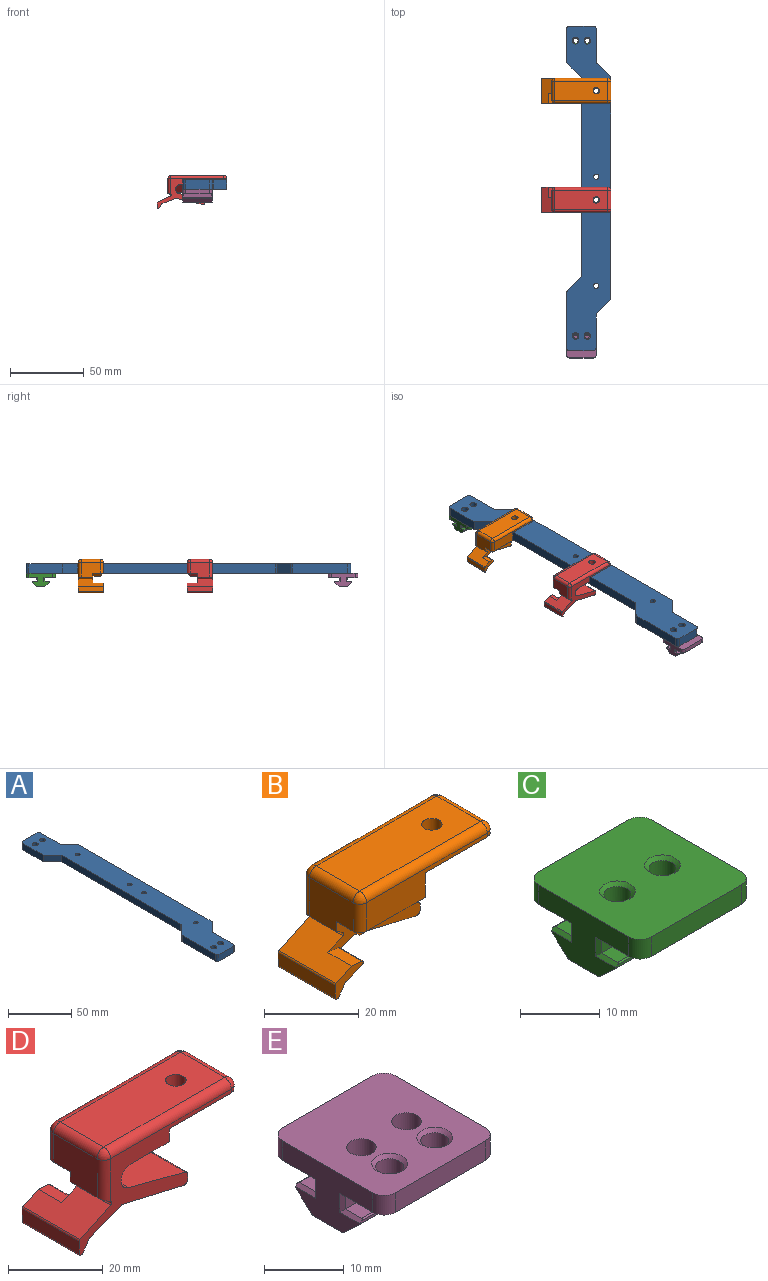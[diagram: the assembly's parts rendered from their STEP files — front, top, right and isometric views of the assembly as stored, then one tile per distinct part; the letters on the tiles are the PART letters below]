
ASSEMBLY  parts=5 mates=4
PART A: 32 faces, bbox 30x220x6.4 mm
  f0: plane 22.9x6.35mm, normal (-1,0,0), area 145.4mm2, adj f8,f9,f20,f31
  f1: plane 16x6.35mm, normal (0,-1,0), area 101.6mm2, adj f8,f9,f16,f17
  f2: plane 22.17x6.35mm, normal (1,0,0), area 140.8mm2, adj f8,f9,f16,f21
  f3: plane 148.34x6.35mm, normal (1,0,0), area 942mm2, adj f8,f9,f13,f14
  f4: plane 22.17x6.35mm, normal (1,0,0), area 140.8mm2, adj f8,f9,f18,f19
  f5: plane 16x6.35mm, normal (0,1,0), area 101.6mm2, adj f8,f9,f19,f20
  f6: plane 134.27x6.35mm, normal (-1,0,0), area 852.6mm2, adj f8,f9,f15,f31
  f7: plane 37.17x6.35mm, normal (-1,0,0), area 236mm2, adj f8,f9,f17,f22
  f8: plane 220x30mm, normal (0,0,1), area 4443.5mm2, adj f0,f1,f2,f3,f4,f5,f6,f7
  f9: plane 220x30mm, normal (0,0,-1), area 4443.5mm2, adj f0,f1,f2,f3,f4,f5,f6,f7
  f10: plane 8.83x8.83mm, normal (-0.71,0.71,0), area 79.3mm2, adj f8,f9,f15,f22
  f11: plane 8.83x8.83mm, normal (0.71,-0.71,0), area 79.3mm2, adj f8,f9,f13,f21
  f12: plane 8.83x8.83mm, normal (0.71,0.71,0), area 79.3mm2, adj f8,f9,f14,f18
  f13: cylinder r=2mm len=6.35mm, axis (0,0,1), area 10mm2, adj f3,f8,f9,f11
  f14: cylinder r=2mm len=6.35mm, axis (0,0,1), area 10mm2, adj f3,f8,f9,f12
  f15: cylinder r=2mm len=6.35mm, axis (0,0,1), area 10mm2, adj f6,f8,f9,f10
  f16: cylinder r=2mm len=6.35mm, axis (0,0,1), area 19.9mm2, adj f1,f2,f8,f9
  f17: cylinder r=2mm len=6.35mm, axis (0,0,-1), area 19.9mm2, adj f1,f7,f8,f9
  f18: cylinder r=2mm len=6.35mm, axis (0,0,1), area 10mm2, adj f4,f8,f9,f12
  f19: cylinder r=2mm len=6.35mm, axis (0,0,-1), area 19.9mm2, adj f4,f5,f8,f9
  f20: cylinder r=2mm len=6.35mm, axis (0,0,1), area 19.9mm2, adj f0,f5,f8,f9
  f21: cylinder r=2mm len=6.35mm, axis (0,0,-1), area 10mm2, adj f2,f8,f9,f11
  f22: cylinder r=2mm len=6.35mm, axis (0,0,1), area 10mm2, adj f7,f8,f9,f10
  f23: cylinder r=2.25mm len=6.35mm, axis (0,0,1), area 89.8mm2, adj f8,f9
  f24: cylinder r=2.25mm len=6.35mm, axis (0,0,1), area 89.8mm2, adj f8,f9
  f25: cylinder r=2.25mm len=6.35mm, axis (0,0,1), area 89.8mm2, adj f8,f9
  f26: cylinder r=2.25mm len=6.35mm, axis (0,0,1), area 89.8mm2, adj f8,f9
  f27: cylinder r=1.75mm len=6.35mm, axis (0,0,1), area 69.8mm2, adj f8,f9
  f28: cylinder r=1.75mm len=6.35mm, axis (0,0,1), area 69.8mm2, adj f8,f9
  f29: cylinder r=1.75mm len=6.35mm, axis (0,0,1), area 69.8mm2, adj f8,f9
  f30: cylinder r=1.75mm len=6.35mm, axis (0,0,1), area 69.8mm2, adj f8,f9
  f31: plane 10x10mm, normal (-0.71,-0.71,0), area 89.8mm2, adj f0,f6,f8,f9
PART B: 50 faces, bbox 47.4x17x22.5 mm
  f0: cylinder r=3mm len=10mm, axis (0,-1,0), area 37mm2, adj f1,f2,f8,f14,f49
  f1: cylinder r=3mm len=7.97mm, axis (0,1,0), area 28.5mm2, adj f0,f9,f14,f49
  f2: plane 27.5x10.44mm, normal (0,-1,0), area 96.4mm2, adj f0,f3,f4,f5,f6,f7,f8,f30
  f3: plane 15.5x5mm, normal (0,0,-1), area 77.5mm2, adj f2,f45,f46,f48,f49
  f4: plane 13x10mm, normal (-1,0,0), area 116.8mm2, adj f2,f5,f16,f20,f43,f45
  f5: plane 10x2.02mm, normal (-0.47,0,-0.88), area 21.9mm2, adj f2,f4,f14,f16,f37
  f6: plane 18.32x10mm, normal (-0.23,0,-0.97), area 188mm2, adj f2,f14,f36,f41
  f7: plane 10x1.26mm, normal (1,0,0), area 12.6mm2, adj f2,f14,f41,f42
  f8: plane 16.82x10mm, normal (0.25,0,0.97), area 173.8mm2, adj f0,f2,f14,f42
  f9: plane 11.31x5mm, normal (0,0,-1), area 56.6mm2, adj f1,f10,f14,f49
  f10: plane 17x6.35mm, normal (1,0,0), area 88.5mm2, adj f9,f11,f14,f15,f46,f49
  f11: plane 20.5x17mm, normal (0,0,-1), area 332.3mm2, adj f10,f12,f14,f15,f18,f25,f26
  f12: plane 13x1mm, normal (1,0,0), area 13mm2, adj f11,f18,f22,f25
  f13: plane 36x13mm, normal (0,0,1), area 453.5mm2, adj f19,f20,f22,f23,f26
  f14: plane 45.37x20.48mm, normal (0,1,0), area 226.8mm2, adj f0,f1,f5,f6,f7,f8,f9,f10
  f15: plane 36x7.35mm, normal (0,-1,0), area 147.1mm2, adj f10,f11,f23,f25,f43,f48
  f16: cylinder r=2mm len=11.07mm, axis (0,0,-1), area 32.6mm2, adj f4,f5,f14,f17
  f17: sphere r=2mm, area 6.3mm2, adj f16,f19,f20
  f18: cylinder r=2mm len=2mm, axis (0,0,1), area 3.1mm2, adj f11,f12,f14,f21
  f19: cylinder r=2mm len=36mm, axis (-1,0,0), area 113.1mm2, adj f13,f14,f17,f21
  f20: cylinder r=2mm len=13mm, axis (0,1,0), area 40.8mm2, adj f4,f13,f17,f44
  f21: sphere r=2mm, area 6.3mm2, adj f18,f19,f22
  f22: cylinder r=2mm len=13mm, axis (0,-1,0), area 40.8mm2, adj f12,f13,f21,f24
  f23: cylinder r=2mm len=36mm, axis (-1,0,0), area 113.1mm2, adj f13,f15,f24,f44
  f24: sphere r=2mm, area 6.3mm2, adj f22,f23,f25
  f25: cylinder r=2mm len=2mm, axis (0,0,1), area 3.1mm2, adj f11,f12,f15,f24
  f26: cylinder r=2.15mm len=4.3mm, axis (0,0,1), area 40.5mm2, adj f11,f13
  f27: plane 17x3.29mm, normal (-1,0,0), area 55.9mm2, adj f14,f32,f33,f38
  f28: plane 17x0.23mm, normal (0,0,-1), area 4mm2, adj f14,f33,f34,f38
  f29: plane 17x2.84mm, normal (0.83,0,-0.56), area 58.4mm2, adj f14,f34,f35,f38
  f30: plane 17x9.08mm, normal (-0.43,0,0.9), area 135.8mm2, adj f2,f14,f32,f37,f38,f39
  f31: plane 17x9.23mm, normal (0.37,0,-0.93), area 135.5mm2, adj f2,f14,f35,f36,f38,f40
  f32: cylinder r=0.5mm len=17mm, axis (0,1,0), area 9.6mm2, adj f14,f27,f30,f38
  f33: cylinder r=0.5mm len=17mm, axis (0,1,0), area 13.4mm2, adj f14,f27,f28,f38
  f34: cylinder r=0.5mm len=17mm, axis (0,1,0), area 8.3mm2, adj f14,f28,f29,f38
  f35: cylinder r=0.5mm len=17mm, axis (0,-1,0), area 5.1mm2, adj f14,f29,f31,f38
  f36: cylinder r=0.5mm len=10mm, axis (0,-1,0), area 3.1mm2, adj f2,f6,f14,f31
  f37: cylinder r=0.5mm len=10mm, axis (0,-1,0), area 11.1mm2, adj f2,f5,f14,f30
  f38: plane 8.39x6.39mm, normal (0,-1,0), area 21.8mm2, adj f27,f28,f29,f30,f31,f32,f33,f34
  f39: plane 7x3.07mm, normal (0.09,0,1), area 21.6mm2, adj f2,f30,f38,f40
  f40: cylinder r=0.5mm len=7mm, axis (0,1,0), area 9.4mm2, adj f2,f31,f38,f39
  f41: cylinder r=1mm len=10mm, axis (0,1,0), area 18mm2, adj f2,f6,f7,f14
  f42: cylinder r=1mm len=10mm, axis (0,1,0), area 13.2mm2, adj f2,f7,f8,f14
  f43: cylinder r=2mm len=7.35mm, axis (0,0,1), area 23.1mm2, adj f4,f15,f44,f47
  f44: sphere r=2mm, area 6.3mm2, adj f20,f23,f43
  f45: plane 5x2mm, normal (-0.71,0,-0.71), area 14.1mm2, adj f2,f3,f4,f47
  f46: plane 9x2mm, normal (0.71,0,-0.71), area 19.8mm2, adj f3,f10,f48,f49
  f47: cone r=2mm half-angle=45deg, axis (0,0,1), area 4.4mm2, adj f43,f45,f48
  f48: plane 17.5x2mm, normal (0,-0.71,-0.71), area 46.7mm2, adj f3,f15,f46,f47
  f49: plane 14.31x5mm, normal (0,0.71,-0.71), area 94.9mm2, adj f0,f1,f3,f9,f10,f46
PART C: 38 faces, bbox 20x20x8.8 mm
  f0: plane 20x7.85mm, normal (0,0,-1), area 145.5mm2, adj f1,f13,f14,f15,f24,f26,f28,f31
  f1: plane 19x2.4mm, normal (0,-1,0), area 45.6mm2, adj f0,f2,f28,f31
  f2: plane 19x2.9mm, normal (0,0,1), area 55.1mm2, adj f1,f16,f35,f36
  f3: plane 20x0.31mm, normal (0,-1,0), area 6.2mm2, adj f14,f15,f16,f17,f35,f36
  f4: plane 20x2.88mm, normal (0,-0.68,-0.73), area 78.8mm2, adj f14,f15,f17,f18
  f5: plane 20x5.34mm, normal (0,0,-1), area 87.6mm2, adj f14,f15,f18,f19,f22,f23
  f6: plane 20x2.88mm, normal (0,0.68,-0.73), area 78.8mm2, adj f14,f15,f19,f20
  f7: plane 20x0.31mm, normal (0,1,0), area 6.2mm2, adj f14,f15,f20,f21,f34,f37
  f8: plane 19x2.9mm, normal (0,0,1), area 55.1mm2, adj f9,f21,f34,f37
  f9: plane 19x2.4mm, normal (0,1,0), area 45.6mm2, adj f8,f10,f29,f30
  f10: plane 20x7.85mm, normal (0,0,-1), area 145.5mm2, adj f9,f11,f14,f15,f25,f27,f29,f30
  f11: plane 16x3mm, normal (0,1,0), area 48mm2, adj f10,f12,f25,f27
  f12: plane 20x20mm, normal (0,0,1), area 364.8mm2, adj f11,f13,f14,f15,f24,f25,f26,f27
  f13: plane 16x3mm, normal (0,-1,0), area 48mm2, adj f0,f12,f24,f26
  f14: plane 16x8.8mm, normal (1,0,0), area 85.4mm2, adj f0,f3,f4,f5,f6,f7,f10,f12
  f15: plane 16x8.8mm, normal (-1,0,0), area 85.4mm2, adj f0,f3,f4,f5,f6,f7,f10,f12
  f16: cylinder r=0.2mm len=19.4mm, axis (-1,0,0), area 6mm2, adj f2,f3,f35,f36
  f17: cylinder r=0.2mm len=20mm, axis (-1,0,0), area 3.3mm2, adj f3,f4,f14,f15
  f18: cylinder r=0.2mm len=20mm, axis (-1,0,0), area 3mm2, adj f4,f5,f14,f15
  f19: cylinder r=0.2mm len=20mm, axis (-1,0,0), area 3mm2, adj f5,f6,f14,f15
  f20: cylinder r=0.2mm len=20mm, axis (-1,0,0), area 3.3mm2, adj f6,f7,f14,f15
  f21: cylinder r=0.2mm len=19.4mm, axis (-1,0,0), area 6mm2, adj f7,f8,f34,f37
  f22: cylinder r=1.75mm len=8.3mm, axis (0,0,1), area 91.3mm2, adj f5,f33
  f23: cylinder r=1.75mm len=8.3mm, axis (0,0,1), area 91.3mm2, adj f5,f32
  f24: cylinder r=2mm len=3mm, axis (0,0,-1), area 9.4mm2, adj f0,f12,f13,f15
  f25: cylinder r=2mm len=3mm, axis (0,0,1), area 9.4mm2, adj f10,f11,f12,f15
  f26: cylinder r=2mm len=3mm, axis (0,0,1), area 9.4mm2, adj f0,f12,f13,f14
  f27: cylinder r=2mm len=3mm, axis (0,0,-1), area 9.4mm2, adj f10,f11,f12,f14
  f28: plane 2.9x0.5mm, normal (-0.71,-0.71,0), area 1.9mm2, adj f0,f1,f15,f35
  f29: plane 2.9x0.5mm, normal (-0.71,0.71,0), area 1.9mm2, adj f9,f10,f15,f34
  f30: plane 2.9x0.5mm, normal (0.71,0.71,0), area 1.9mm2, adj f9,f10,f14,f37
  f31: plane 2.9x0.5mm, normal (0.71,-0.71,0), area 1.9mm2, adj f0,f1,f14,f36
  f32: cone r=1.75mm half-angle=45deg, axis (0,0,1), area 8.9mm2, adj f12,f23
  f33: cone r=1.75mm half-angle=45deg, axis (0,0,1), area 8.9mm2, adj f12,f22
  f34: plane 3.6x0.5mm, normal (-0.71,0,0.71), area 2.4mm2, adj f7,f8,f15,f21,f29
  f35: plane 3.6x0.5mm, normal (-0.71,0,0.71), area 2.4mm2, adj f2,f3,f15,f16,f28
  f36: plane 3.6x0.5mm, normal (0.71,0,0.71), area 2.4mm2, adj f2,f3,f14,f16,f31
  f37: plane 3.6x0.5mm, normal (0.71,0,0.71), area 2.4mm2, adj f7,f8,f14,f21,f30
PART D: 50 faces, bbox 47.4x17x22.5 mm
  f0: cylinder r=3mm len=7.97mm, axis (0,-1,0), area 28.5mm2, adj f1,f9,f14,f49
  f1: cylinder r=3mm len=10mm, axis (0,1,0), area 37mm2, adj f0,f2,f8,f14,f49
  f2: plane 27.5x10.44mm, normal (0,1,0), area 96.4mm2, adj f1,f3,f4,f5,f6,f7,f8,f30
  f3: plane 15.5x5mm, normal (0,0,-1), area 77.5mm2, adj f2,f45,f46,f48,f49
  f4: plane 13x10mm, normal (-1,0,0), area 116.7mm2, adj f2,f5,f16,f20,f43,f45
  f5: plane 10x2.02mm, normal (-0.47,0,-0.88), area 21.9mm2, adj f2,f4,f14,f16,f37
  f6: plane 18.32x10mm, normal (-0.23,0,-0.97), area 188mm2, adj f2,f14,f36,f41
  f7: plane 10x1.26mm, normal (1,0,0), area 12.6mm2, adj f2,f14,f41,f42
  f8: plane 16.82x10mm, normal (0.25,0,0.97), area 173.8mm2, adj f1,f2,f14,f42
  f9: plane 11.31x5mm, normal (0,0,-1), area 56.6mm2, adj f0,f10,f14,f49
  f10: plane 17x6.35mm, normal (1,0,0), area 88.4mm2, adj f9,f11,f14,f15,f46,f49
  f11: plane 20.5x17mm, normal (0,0,-1), area 332.3mm2, adj f10,f12,f14,f15,f18,f25,f26
  f12: plane 13x1mm, normal (1,0,0), area 13mm2, adj f11,f18,f22,f25
  f13: plane 36x13mm, normal (0,0,1), area 453.5mm2, adj f19,f20,f22,f23,f26
  f14: plane 45.37x20.48mm, normal (0,-1,0), area 226.8mm2, adj f0,f1,f5,f6,f7,f8,f9,f10
  f15: plane 36x7.35mm, normal (0,1,0), area 147.1mm2, adj f10,f11,f23,f25,f43,f48
  f16: cylinder r=2mm len=11.07mm, axis (0,0,-1), area 32.6mm2, adj f4,f5,f14,f17
  f17: sphere r=2mm, area 6.3mm2, adj f16,f19,f20
  f18: cylinder r=2mm len=2mm, axis (0,0,1), area 3.1mm2, adj f11,f12,f14,f21
  f19: cylinder r=2mm len=36mm, axis (-1,0,0), area 113.1mm2, adj f13,f14,f17,f21
  f20: cylinder r=2mm len=13mm, axis (0,-1,0), area 40.8mm2, adj f4,f13,f17,f44
  f21: sphere r=2mm, area 6.3mm2, adj f18,f19,f22
  f22: cylinder r=2mm len=13mm, axis (0,1,0), area 40.8mm2, adj f12,f13,f21,f24
  f23: cylinder r=2mm len=36mm, axis (-1,0,0), area 113.1mm2, adj f13,f15,f24,f44
  f24: sphere r=2mm, area 6.3mm2, adj f22,f23,f25
  f25: cylinder r=2mm len=2mm, axis (0,0,1), area 3.1mm2, adj f11,f12,f15,f24
  f26: cylinder r=2.15mm len=4.3mm, axis (0,0,1), area 40.5mm2, adj f11,f13
  f27: plane 17x3.29mm, normal (-1,0,0), area 55.9mm2, adj f14,f32,f33,f38
  f28: plane 17x0.23mm, normal (0,0,-1), area 4mm2, adj f14,f33,f34,f38
  f29: plane 17x2.84mm, normal (0.83,0,-0.56), area 58.4mm2, adj f14,f34,f35,f38
  f30: plane 17x9.08mm, normal (-0.43,0,0.9), area 135.8mm2, adj f2,f14,f32,f37,f38,f39
  f31: plane 17x9.23mm, normal (0.37,0,-0.93), area 135.5mm2, adj f2,f14,f35,f36,f38,f40
  f32: cylinder r=0.5mm len=17mm, axis (0,-1,0), area 9.6mm2, adj f14,f27,f30,f38
  f33: cylinder r=0.5mm len=17mm, axis (0,-1,0), area 13.4mm2, adj f14,f27,f28,f38
  f34: cylinder r=0.5mm len=17mm, axis (0,-1,0), area 8.3mm2, adj f14,f28,f29,f38
  f35: cylinder r=0.5mm len=17mm, axis (0,1,0), area 5.1mm2, adj f14,f29,f31,f38
  f36: cylinder r=0.5mm len=10mm, axis (0,1,0), area 3.1mm2, adj f2,f6,f14,f31
  f37: cylinder r=0.5mm len=10mm, axis (0,1,0), area 11.1mm2, adj f2,f5,f14,f30
  f38: plane 8.39x6.39mm, normal (0,1,0), area 21.8mm2, adj f27,f28,f29,f30,f31,f32,f33,f34
  f39: plane 7x3.07mm, normal (0.09,0,1), area 21.6mm2, adj f2,f30,f38,f40
  f40: cylinder r=0.5mm len=7mm, axis (0,-1,0), area 9.4mm2, adj f2,f31,f38,f39
  f41: cylinder r=1mm len=10mm, axis (0,-1,0), area 18mm2, adj f2,f6,f7,f14
  f42: cylinder r=1mm len=10mm, axis (0,-1,0), area 13.2mm2, adj f2,f7,f8,f14
  f43: cylinder r=2mm len=7.35mm, axis (0,0,-1), area 23.1mm2, adj f4,f15,f44,f47
  f44: sphere r=2mm, area 6.3mm2, adj f20,f23,f43
  f45: plane 5x2mm, normal (-0.71,0,-0.71), area 14.1mm2, adj f2,f3,f4,f47
  f46: plane 9x2mm, normal (0.71,0,-0.71), area 19.8mm2, adj f3,f10,f48,f49
  f47: cone r=2mm half-angle=45deg, axis (0,0,1), area 4.4mm2, adj f43,f45,f48
  f48: plane 17.5x2mm, normal (0,0.71,-0.71), area 46.7mm2, adj f3,f15,f46,f47
  f49: plane 14.31x5mm, normal (0,-0.71,-0.71), area 94.9mm2, adj f0,f1,f3,f9,f10,f46
PART E: 40 faces, bbox 20x20x8.8 mm
  f0: plane 20x7.85mm, normal (0,0,-1), area 126.3mm2, adj f1,f13,f14,f15,f22,f23,f24,f26
  f1: plane 19x2.4mm, normal (0,-1,0), area 45.6mm2, adj f0,f2,f28,f31
  f2: plane 19x2.9mm, normal (0,0,1), area 55.1mm2, adj f1,f16,f35,f36
  f3: plane 20x0.31mm, normal (0,-1,0), area 6.2mm2, adj f14,f15,f16,f17,f35,f36
  f4: plane 20x2.88mm, normal (0,-0.68,-0.73), area 78.8mm2, adj f14,f15,f17,f18
  f5: plane 20x5.34mm, normal (0,0,-1), area 85.3mm2, adj f14,f15,f18,f19,f38,f39
  f6: plane 20x2.88mm, normal (0,0.68,-0.73), area 78.8mm2, adj f14,f15,f19,f20
  f7: plane 20x0.31mm, normal (0,1,0), area 6.2mm2, adj f14,f15,f20,f21,f34,f37
  f8: plane 19x2.9mm, normal (0,0,1), area 55.1mm2, adj f9,f21,f34,f37
  f9: plane 19x2.4mm, normal (0,1,0), area 45.6mm2, adj f8,f10,f29,f30
  f10: plane 20x7.85mm, normal (0,0,-1), area 145.5mm2, adj f9,f11,f14,f15,f25,f27,f29,f30
  f11: plane 16x3mm, normal (0,1,0), area 48mm2, adj f10,f12,f25,f27
  f12: plane 20x20mm, normal (0,0,1), area 343.3mm2, adj f11,f13,f14,f15,f24,f25,f26,f27
  f13: plane 16x3mm, normal (0,-1,0), area 48mm2, adj f0,f12,f24,f26
  f14: plane 16x8.8mm, normal (1,0,0), area 85.4mm2, adj f0,f3,f4,f5,f6,f7,f10,f12
  f15: plane 16x8.8mm, normal (-1,0,0), area 85.4mm2, adj f0,f3,f4,f5,f6,f7,f10,f12
  f16: cylinder r=0.2mm len=19.4mm, axis (-1,0,0), area 6mm2, adj f2,f3,f35,f36
  f17: cylinder r=0.2mm len=20mm, axis (-1,0,0), area 3.3mm2, adj f3,f4,f14,f15
  f18: cylinder r=0.2mm len=20mm, axis (-1,0,0), area 3mm2, adj f4,f5,f14,f15
  f19: cylinder r=0.2mm len=20mm, axis (-1,0,0), area 3mm2, adj f5,f6,f14,f15
  f20: cylinder r=0.2mm len=20mm, axis (-1,0,0), area 3.3mm2, adj f6,f7,f14,f15
  f21: cylinder r=0.2mm len=19.4mm, axis (-1,0,0), area 6mm2, adj f7,f8,f34,f37
  f22: cylinder r=1.75mm len=3.5mm, axis (0,0,1), area 27.5mm2, adj f0,f33
  f23: cylinder r=1.75mm len=3.5mm, axis (0,0,1), area 27.5mm2, adj f0,f32
  f24: cylinder r=2mm len=3mm, axis (0,0,-1), area 9.4mm2, adj f0,f12,f13,f15
  f25: cylinder r=2mm len=3mm, axis (0,0,1), area 9.4mm2, adj f10,f11,f12,f15
  f26: cylinder r=2mm len=3mm, axis (0,0,1), area 9.4mm2, adj f0,f12,f13,f14
  f27: cylinder r=2mm len=3mm, axis (0,0,-1), area 9.4mm2, adj f10,f11,f12,f14
  f28: plane 2.9x0.5mm, normal (-0.71,-0.71,0), area 1.9mm2, adj f0,f1,f15,f35
  f29: plane 2.9x0.5mm, normal (-0.71,0.71,0), area 1.9mm2, adj f9,f10,f15,f34
  f30: plane 2.9x0.5mm, normal (0.71,0.71,0), area 1.9mm2, adj f9,f10,f14,f37
  f31: plane 2.9x0.5mm, normal (0.71,-0.71,0), area 1.9mm2, adj f0,f1,f14,f36
  f32: cone r=1.75mm half-angle=45deg, axis (0,0,1), area 8.9mm2, adj f12,f23
  f33: cone r=1.75mm half-angle=45deg, axis (0,0,1), area 8.9mm2, adj f12,f22
  f34: plane 3.6x0.5mm, normal (-0.71,0,0.71), area 2.4mm2, adj f7,f8,f15,f21,f29
  f35: plane 3.6x0.5mm, normal (-0.71,0,0.71), area 2.4mm2, adj f2,f3,f15,f16,f28
  f36: plane 3.6x0.5mm, normal (0.71,0,0.71), area 2.4mm2, adj f2,f3,f14,f16,f31
  f37: plane 3.6x0.5mm, normal (0.71,0,0.71), area 2.4mm2, adj f7,f8,f14,f21,f30
  f38: cylinder r=1.85mm len=8.8mm, axis (0,0,1), area 102.3mm2, adj f5,f12
  f39: cylinder r=1.85mm len=8.8mm, axis (0,0,1), area 102.3mm2, adj f5,f12
PLACE A t=(3.46,-65.07,32.74)mm fixed
PLACE B t=(3.46,-65.07,32.74)mm
PLACE C t=(3.46,134.93,32.74)mm
PLACE D t=(3.46,-65.07,32.74)mm
PLACE E rot(axis=(0,0,-1),180deg) t=(23.46,-70.07,32.74)mm
MATE fastened A.f23 <-> C.f32  axis (0,0,-1) through (17.46,134.93,34.24)mm
MATE fastened B.f26 <-> A.f27  axis (0,0,-1) through (23.46,101.03,40.59)mm
MATE fastened A.f25 <-> E.f33  axis (0,0,-1) through (17.46,-65.07,34.24)mm
MATE fastened D.f26 <-> A.f28  axis (0,0,-1) through (23.46,27.03,40.59)mm
